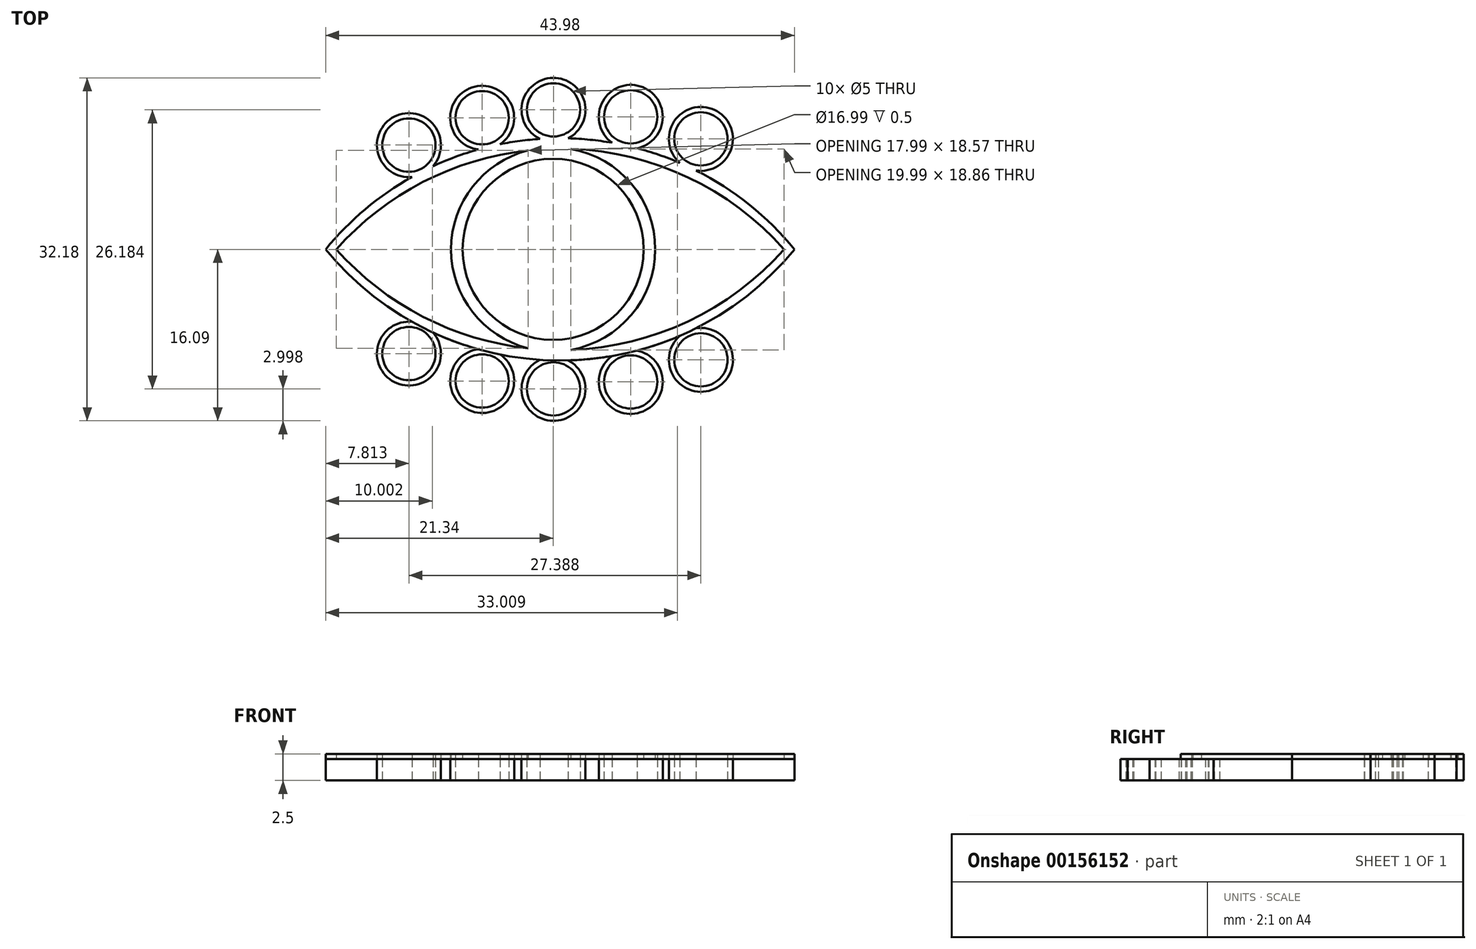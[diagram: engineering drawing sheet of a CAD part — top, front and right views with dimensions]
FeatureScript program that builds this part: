
annotation { "Feature Type Name" : "Feature", "Feature Type Description" : "" }
export const myFeature = defineFeature(function(context is Context, id is Id, definition is map)
    precondition{}
    {
        {
            var Q0;
            Q0=qCreatedBy(makeId("Top.planeOp"),FACE);
            var sketch = newSketch(context, id + "F0", { "sketchPlane" : qUnion([Q0])});
            skArc(sketch, "E0", {"start": v(-11.27, 7.8) * mm, "mid": v(-14.9, 12.45) * mm, "end": v(-13.24, 6.8) * mm});
            skCircle(sketch, "E1", {"center": v(-13.53, 9.78) * mm, "radius": 2.5 * mm});
            skArc(sketch, "E2", {"start": v(22.66, -0.03) * mm, "mid": v(0.67, 10.43) * mm, "end": v(-21.34, 0) * mm});
            skArc(sketch, "E3", {"start": v(-4.98, 9.86) * mm, "mid": v(-7.36, 15.27) * mm, "end": v(-7.01, 9.37) * mm});
            skArc(sketch, "E4", {"start": v(1.4, 10.42) * mm, "mid": v(-0.02, 16.1) * mm, "end": v(-1.22, 10.37) * mm});
            skArc(sketch, "E5", {"start": v(7.87, 9.5) * mm, "mid": v(7.92, 15.37) * mm, "end": v(5.52, 10) * mm});
            skArc(sketch, "E6", {"start": v(13.4, 7.4) * mm, "mid": v(15.13, 13.09) * mm, "end": v(11.88, 8.11) * mm});
            skCircle(sketch, "E7", {"center": v(-6.66, 12.35) * mm, "radius": 2.5 * mm});
            skCircle(sketch, "E8", {"center": v(0.04, 13.1) * mm, "radius": 2.5 * mm});
            skCircle(sketch, "E9", {"center": v(7.28, 12.44) * mm, "radius": 2.5 * mm});
            skCircle(sketch, "E10", {"center": v(13.86, 10.37) * mm, "radius": 2.5 * mm});
            skArc(sketch, "E11.MirrorCS", {"start": v(22.66, 0.03) * mm, "mid": v(0.67, -10.43) * mm, "end": v(-21.34, 0) * mm});
            skArc(sketch, "E12.MirrorC", {"start": v(-11.27, -7.8) * mm, "mid": v(-14.9, -12.45) * mm, "end": v(-13.24, -6.8) * mm});
            skCircle(sketch, "E13.MirrorC", {"center": v(-13.53, -9.78) * mm, "radius": 2.5 * mm});
            skArc(sketch, "E14.MirrorC", {"start": v(-4.98, -9.86) * mm, "mid": v(-7.36, -15.27) * mm, "end": v(-7.01, -9.37) * mm});
            skCircle(sketch, "E15.MirrorC", {"center": v(-6.66, -12.35) * mm, "radius": 2.5 * mm});
            skArc(sketch, "E16.MirrorC", {"start": v(1.4, -10.42) * mm, "mid": v(-0.02, -16.1) * mm, "end": v(-1.22, -10.37) * mm});
            skCircle(sketch, "E17.MirrorC", {"center": v(0.04, -13.1) * mm, "radius": 2.5 * mm});
            skArc(sketch, "E18.MirrorC", {"start": v(7.87, -9.5) * mm, "mid": v(7.92, -15.37) * mm, "end": v(5.52, -10) * mm});
            skCircle(sketch, "E19.MirrorC", {"center": v(7.28, -12.44) * mm, "radius": 2.5 * mm});
            skArc(sketch, "E20.MirrorC", {"start": v(13.4, -7.4) * mm, "mid": v(15.13, -13.09) * mm, "end": v(11.88, -8.11) * mm});
            skCircle(sketch, "E21.MirrorC", {"center": v(13.86, -10.37) * mm, "radius": 2.5 * mm});
            skLineSegment(sketch, "E22", {"start": v(-20.34, 18.05) * mm, "end": v(-20.34, -19.56) * mm, "construction": true});
            skLineSegment(sketch, "E23", {"start": v(21.66, 18.36) * mm, "end": v(21.66, -18.85) * mm, "construction": true});
            skLineSegment(sketch, "E24", {"start": v(-24.04, 9.43) * mm, "end": v(-0.49, 9.43) * mm, "construction": true});
            skPoint(sketch, "E25.startSnap0", {"position": v(21.66, -0.25) * mm});
            skLineSegment(sketch, "E26.trimOffspring", {"start": v(0.65, 9.43) * mm, "end": v(29.58, 9.43) * mm, "construction": true});
            skArc(sketch, "E27", {"start": v(21.66, 0) * mm, "mid": v(0.66, 9.45) * mm, "end": v(-20.34, 0) * mm});
            skArc(sketch, "E28.MirrorCS", {"start": v(21.66, 0) * mm, "mid": v(0.66, -9.45) * mm, "end": v(-20.34, 0) * mm});
            skArc(sketch, "E29", {"start": v(-2.34, 9.28) * mm, "mid": v(-9.58, 0) * mm, "end": v(-2.34, -9.28) * mm});
            skCircle(sketch, "E30", {"center": v(0, 0) * mm, "radius": 8.5 * mm});
            skArc(sketch, "E31.trimOffspring", {"start": v(1.67, -9.43) * mm, "mid": v(9.58, 0) * mm, "end": v(1.67, 9.43) * mm});
            skSolve(sketch);
        }
        {
            var Q0;
            {var subQ7=sQuery(id+"F0.wireOp",EDGE,"E2");var subQ22=sQuery(id+"F0.wireOp",EDGE,"E6");var subQ31=makeQuery(id+"F0.imprint","INTERSECT",VERTEX,{"disambiguationData":[OD(0.0)],"derivedFrom":[subQ7,subQ22]});Q0=makeQuery(id+"F0.imprint","IMPRINT",FACE,{"disambiguationData":[TD([[makeQuery(id+"F0.imprint","IMPRINT",EDGE,{"disambiguationData":[TD([[subQ31,1.0]])],"derivedFrom":subQ7}),1.0]])]});}
            var Q1;
            {var subQ0=sQuery(id+"F0.wireOp",EDGE,"E29");Q1=makeQuery(id+"F0.imprint","IMPRINT",FACE,{"disambiguationData":[TD([[makeQuery(id+"F0.imprint","IMPRINT",EDGE,{"derivedFrom":subQ0}),1.0]])]});}
            var Q2;
            {var subQ0=sQuery(id+"F0.wireOp",EDGE,"E20.MirrorC");Q2=makeQuery(id+"F0.imprint","IMPRINT",FACE,{"disambiguationData":[TD([[makeQuery(id+"F0.imprint","IMPRINT",EDGE,{"derivedFrom":subQ0}),-1.0]])]});}
            var Q3;
            {var subQ0=sQuery(id+"F0.wireOp",EDGE,"E18.MirrorC");Q3=makeQuery(id+"F0.imprint","IMPRINT",FACE,{"disambiguationData":[TD([[makeQuery(id+"F0.imprint","IMPRINT",EDGE,{"derivedFrom":subQ0}),-1.0]])]});}
            var Q4;
            {var subQ0=sQuery(id+"F0.wireOp",EDGE,"E16.MirrorC");Q4=makeQuery(id+"F0.imprint","IMPRINT",FACE,{"disambiguationData":[TD([[makeQuery(id+"F0.imprint","IMPRINT",EDGE,{"derivedFrom":subQ0}),-1.0]])]});}
            var Q5;
            {var subQ0=sQuery(id+"F0.wireOp",EDGE,"E14.MirrorC");Q5=makeQuery(id+"F0.imprint","IMPRINT",FACE,{"disambiguationData":[TD([[makeQuery(id+"F0.imprint","IMPRINT",EDGE,{"derivedFrom":subQ0}),-1.0]])]});}
            var Q6;
            {var subQ0=sQuery(id+"F0.wireOp",EDGE,"E12.MirrorC");Q6=makeQuery(id+"F0.imprint","IMPRINT",FACE,{"disambiguationData":[TD([[makeQuery(id+"F0.imprint","IMPRINT",EDGE,{"derivedFrom":subQ0}),-1.0]])]});}
            var Q7;
            {var subQ0=sQuery(id+"F0.wireOp",EDGE,"E6");Q7=makeQuery(id+"F0.imprint","IMPRINT",FACE,{"disambiguationData":[TD([[makeQuery(id+"F0.imprint","IMPRINT",EDGE,{"derivedFrom":subQ0}),1.0]])]});}
            var Q8;
            {var subQ0=sQuery(id+"F0.wireOp",EDGE,"E5");Q8=makeQuery(id+"F0.imprint","IMPRINT",FACE,{"disambiguationData":[TD([[makeQuery(id+"F0.imprint","IMPRINT",EDGE,{"derivedFrom":subQ0}),1.0]])]});}
            var Q9;
            {var subQ0=sQuery(id+"F0.wireOp",EDGE,"E4");Q9=makeQuery(id+"F0.imprint","IMPRINT",FACE,{"disambiguationData":[TD([[makeQuery(id+"F0.imprint","IMPRINT",EDGE,{"derivedFrom":subQ0}),1.0]])]});}
            var Q10;
            {var subQ0=sQuery(id+"F0.wireOp",EDGE,"E3");Q10=makeQuery(id+"F0.imprint","IMPRINT",FACE,{"disambiguationData":[TD([[makeQuery(id+"F0.imprint","IMPRINT",EDGE,{"derivedFrom":subQ0}),1.0]])]});}
            var Q11;
            {var subQ0=sQuery(id+"F0.wireOp",EDGE,"E0");Q11=makeQuery(id+"F0.imprint","IMPRINT",FACE,{"disambiguationData":[TD([[makeQuery(id+"F0.imprint","IMPRINT",EDGE,{"derivedFrom":subQ0}),1.0]])]});}
            extrude(context, id + "F1", {"entities" : qUnion([Q0, Q1, Q2, Q3, Q4, Q5, Q6, Q7, Q8, Q9, Q10, Q11]), "depth" : .5 * mm});
        }
        {
            var Q0;
            {var subQ0=sQuery(id+"F0.wireOp",EDGE,"E14.MirrorC");Q0=makeQuery(id+"F0.imprint","IMPRINT",FACE,{"disambiguationData":[TD([[makeQuery(id+"F0.imprint","IMPRINT",EDGE,{"derivedFrom":subQ0}),-1.0]])]});}
            var Q1;
            {var subQ3=sQuery(id+"F0.wireOp",EDGE,"E29");Q1=makeQuery(id+"F0.imprint","IMPRINT",FACE,{"disambiguationData":[TD([[makeQuery(id+"F0.imprint","IMPRINT",EDGE,{"derivedFrom":subQ3}),-1.0]])]});}
            var Q2;
            {var subQ0=sQuery(id+"F0.wireOp",EDGE,"E12.MirrorC");Q2=makeQuery(id+"F0.imprint","IMPRINT",FACE,{"disambiguationData":[TD([[makeQuery(id+"F0.imprint","IMPRINT",EDGE,{"derivedFrom":subQ0}),-1.0]])]});}
            var Q3;
            {var subQ0=sQuery(id+"F0.wireOp",EDGE,"E3");Q3=makeQuery(id+"F0.imprint","IMPRINT",FACE,{"disambiguationData":[TD([[makeQuery(id+"F0.imprint","IMPRINT",EDGE,{"derivedFrom":subQ0}),1.0]])]});}
            var Q4;
            {var subQ0=sQuery(id+"F0.wireOp",EDGE,"E5");Q4=makeQuery(id+"F0.imprint","IMPRINT",FACE,{"disambiguationData":[TD([[makeQuery(id+"F0.imprint","IMPRINT",EDGE,{"derivedFrom":subQ0}),1.0]])]});}
            var Q5;
            {var subQ0=sQuery(id+"F0.wireOp",EDGE,"E20.MirrorC");Q5=makeQuery(id+"F0.imprint","IMPRINT",FACE,{"disambiguationData":[TD([[makeQuery(id+"F0.imprint","IMPRINT",EDGE,{"derivedFrom":subQ0}),-1.0]])]});}
            var Q6;
            Q6=makeQuery(id+"F0.imprint","IMPRINT",FACE,{"disambiguationData":[TD([[makeQuery(id+"F0.imprint","IMPRINT",EDGE,{"derivedFrom":sQuery(id+"F0.wireOp",EDGE,"E1")}),1.0]])]});
            var Q7;
            Q7=makeQuery(id+"F0.imprint","IMPRINT",FACE,{"disambiguationData":[TD([[makeQuery(id+"F0.imprint","IMPRINT",EDGE,{"derivedFrom":sQuery(id+"F0.wireOp",EDGE,"E7")}),1.0]])]});
            var Q8;
            Q8=makeQuery(id+"F0.imprint","IMPRINT",FACE,{"disambiguationData":[TD([[makeQuery(id+"F0.imprint","IMPRINT",EDGE,{"derivedFrom":sQuery(id+"F0.wireOp",EDGE,"E8")}),1.0]])]});
            var Q9;
            Q9=makeQuery(id+"F0.imprint","IMPRINT",FACE,{"disambiguationData":[TD([[makeQuery(id+"F0.imprint","IMPRINT",EDGE,{"derivedFrom":sQuery(id+"F0.wireOp",EDGE,"E9")}),1.0]])]});
            var Q10;
            Q10=makeQuery(id+"F0.imprint","IMPRINT",FACE,{"disambiguationData":[TD([[makeQuery(id+"F0.imprint","IMPRINT",EDGE,{"derivedFrom":sQuery(id+"F0.wireOp",EDGE,"E10")}),1.0]])]});
            var Q11;
            Q11=makeQuery(id+"F0.imprint","IMPRINT",FACE,{"disambiguationData":[TD([[makeQuery(id+"F0.imprint","IMPRINT",EDGE,{"derivedFrom":sQuery(id+"F0.wireOp",EDGE,"E13.MirrorC")}),-1.0]])]});
            var Q12;
            Q12=makeQuery(id+"F0.imprint","IMPRINT",FACE,{"disambiguationData":[TD([[makeQuery(id+"F0.imprint","IMPRINT",EDGE,{"derivedFrom":sQuery(id+"F0.wireOp",EDGE,"E15.MirrorC")}),-1.0]])]});
            var Q13;
            Q13=makeQuery(id+"F0.imprint","IMPRINT",FACE,{"disambiguationData":[TD([[makeQuery(id+"F0.imprint","IMPRINT",EDGE,{"derivedFrom":sQuery(id+"F0.wireOp",EDGE,"E17.MirrorC")}),-1.0]])]});
            var Q14;
            Q14=makeQuery(id+"F0.imprint","IMPRINT",FACE,{"disambiguationData":[TD([[makeQuery(id+"F0.imprint","IMPRINT",EDGE,{"derivedFrom":sQuery(id+"F0.wireOp",EDGE,"E19.MirrorC")}),-1.0]])]});
            var Q15;
            Q15=makeQuery(id+"F0.imprint","IMPRINT",FACE,{"disambiguationData":[TD([[makeQuery(id+"F0.imprint","IMPRINT",EDGE,{"derivedFrom":sQuery(id+"F0.wireOp",EDGE,"E21.MirrorC")}),-1.0]])]});
            var Q16;
            Q16=makeQuery(id+"F0.imprint","IMPRINT",FACE,{"disambiguationData":[TD([[makeQuery(id+"F0.imprint","IMPRINT",EDGE,{"derivedFrom":sQuery(id+"F0.wireOp",EDGE,"E30")}),1.0]])]});
            var Q17;
            {var subQ0=sQuery(id+"F0.wireOp",EDGE,"E0");Q17=makeQuery(id+"F0.imprint","IMPRINT",FACE,{"disambiguationData":[TD([[makeQuery(id+"F0.imprint","IMPRINT",EDGE,{"derivedFrom":subQ0}),1.0]])]});}
            var Q18;
            {var subQ0=sQuery(id+"F0.wireOp",EDGE,"E6");Q18=makeQuery(id+"F0.imprint","IMPRINT",FACE,{"disambiguationData":[TD([[makeQuery(id+"F0.imprint","IMPRINT",EDGE,{"derivedFrom":subQ0}),1.0]])]});}
            var Q19;
            {var subQ0=sQuery(id+"F0.wireOp",EDGE,"E29");Q19=makeQuery(id+"F0.imprint","IMPRINT",FACE,{"disambiguationData":[TD([[makeQuery(id+"F0.imprint","IMPRINT",EDGE,{"derivedFrom":subQ0}),1.0]])]});}
            var Q20;
            {var subQ3=sQuery(id+"F0.wireOp",EDGE,"E31.trimOffspring");Q20=makeQuery(id+"F0.imprint","IMPRINT",FACE,{"disambiguationData":[TD([[makeQuery(id+"F0.imprint","IMPRINT",EDGE,{"derivedFrom":subQ3}),-1.0]])]});}
            var Q21;
            {var subQ0=sQuery(id+"F0.wireOp",EDGE,"E18.MirrorC");Q21=makeQuery(id+"F0.imprint","IMPRINT",FACE,{"disambiguationData":[TD([[makeQuery(id+"F0.imprint","IMPRINT",EDGE,{"derivedFrom":subQ0}),-1.0]])]});}
            var Q22;
            {var subQ0=sQuery(id+"F0.wireOp",EDGE,"E16.MirrorC");Q22=makeQuery(id+"F0.imprint","IMPRINT",FACE,{"disambiguationData":[TD([[makeQuery(id+"F0.imprint","IMPRINT",EDGE,{"derivedFrom":subQ0}),-1.0]])]});}
            var Q23;
            {var subQ7=sQuery(id+"F0.wireOp",EDGE,"E2");var subQ22=sQuery(id+"F0.wireOp",EDGE,"E6");var subQ31=makeQuery(id+"F0.imprint","INTERSECT",VERTEX,{"disambiguationData":[OD(0.0)],"derivedFrom":[subQ7,subQ22]});Q23=makeQuery(id+"F0.imprint","IMPRINT",FACE,{"disambiguationData":[TD([[makeQuery(id+"F0.imprint","IMPRINT",EDGE,{"disambiguationData":[TD([[subQ31,1.0]])],"derivedFrom":subQ7}),1.0]])]});}
            var Q24;
            {var subQ0=sQuery(id+"F0.wireOp",EDGE,"E4");Q24=makeQuery(id+"F0.imprint","IMPRINT",FACE,{"disambiguationData":[TD([[makeQuery(id+"F0.imprint","IMPRINT",EDGE,{"derivedFrom":subQ0}),1.0]])]});}
            extrude(context, id + "F2", {"entities" : qUnion([Q0, Q1, Q2, Q3, Q4, Q5, Q6, Q7, Q8, Q9, Q10, Q11, Q12, Q13, Q14, Q15, Q16, Q17, Q18, Q19, Q20, Q21, Q22, Q23, Q24]), "depth" : 2 * mm});
        }
        {
            var Q0;
            Q0=makeQuery(id+"F1.opExtrude","SWEPT_BODY",BODY,{"disambiguationData":[OSD([sQuery(id+"F0.wireOp",EDGE,"E0"),sQuery(id+"F0.wireOp",EDGE,"E1"),sQuery(id+"F0.wireOp",EDGE,"E2"),sQuery(id+"F0.wireOp",EDGE,"E3"),sQuery(id+"F0.wireOp",EDGE,"E4"),sQuery(id+"F0.wireOp",EDGE,"E5"),sQuery(id+"F0.wireOp",EDGE,"E6"),sQuery(id+"F0.wireOp",EDGE,"E7"),sQuery(id+"F0.wireOp",EDGE,"E8"),sQuery(id+"F0.wireOp",EDGE,"E9"),sQuery(id+"F0.wireOp",EDGE,"E10"),sQuery(id+"F0.wireOp",EDGE,"E11.MirrorCS"),sQuery(id+"F0.wireOp",EDGE,"E12.MirrorC"),sQuery(id+"F0.wireOp",EDGE,"E13.MirrorC"),sQuery(id+"F0.wireOp",EDGE,"E14.MirrorC"),sQuery(id+"F0.wireOp",EDGE,"E15.MirrorC"),sQuery(id+"F0.wireOp",EDGE,"E16.MirrorC"),sQuery(id+"F0.wireOp",EDGE,"E17.MirrorC"),sQuery(id+"F0.wireOp",EDGE,"E18.MirrorC"),sQuery(id+"F0.wireOp",EDGE,"E19.MirrorC"),sQuery(id+"F0.wireOp",EDGE,"E20.MirrorC"),sQuery(id+"F0.wireOp",EDGE,"E21.MirrorC"),sQuery(id+"F0.wireOp",EDGE,"E27"),sQuery(id+"F0.wireOp",EDGE,"E28.MirrorCS"),sQuery(id+"F0.wireOp",EDGE,"E29"),sQuery(id+"F0.wireOp",EDGE,"E30"),sQuery(id+"F0.wireOp",EDGE,"E31.trimOffspring")])]});
            transform(context, id + "F3", {"entities" : qUnion([Q0]), "transformType" : TransformType.TRANSLATION_3D, "dx" : 0 * mm, "dy" : 0 * mm, "dz" : 2 * mm, "makeCopy" : false});
        }
    });
